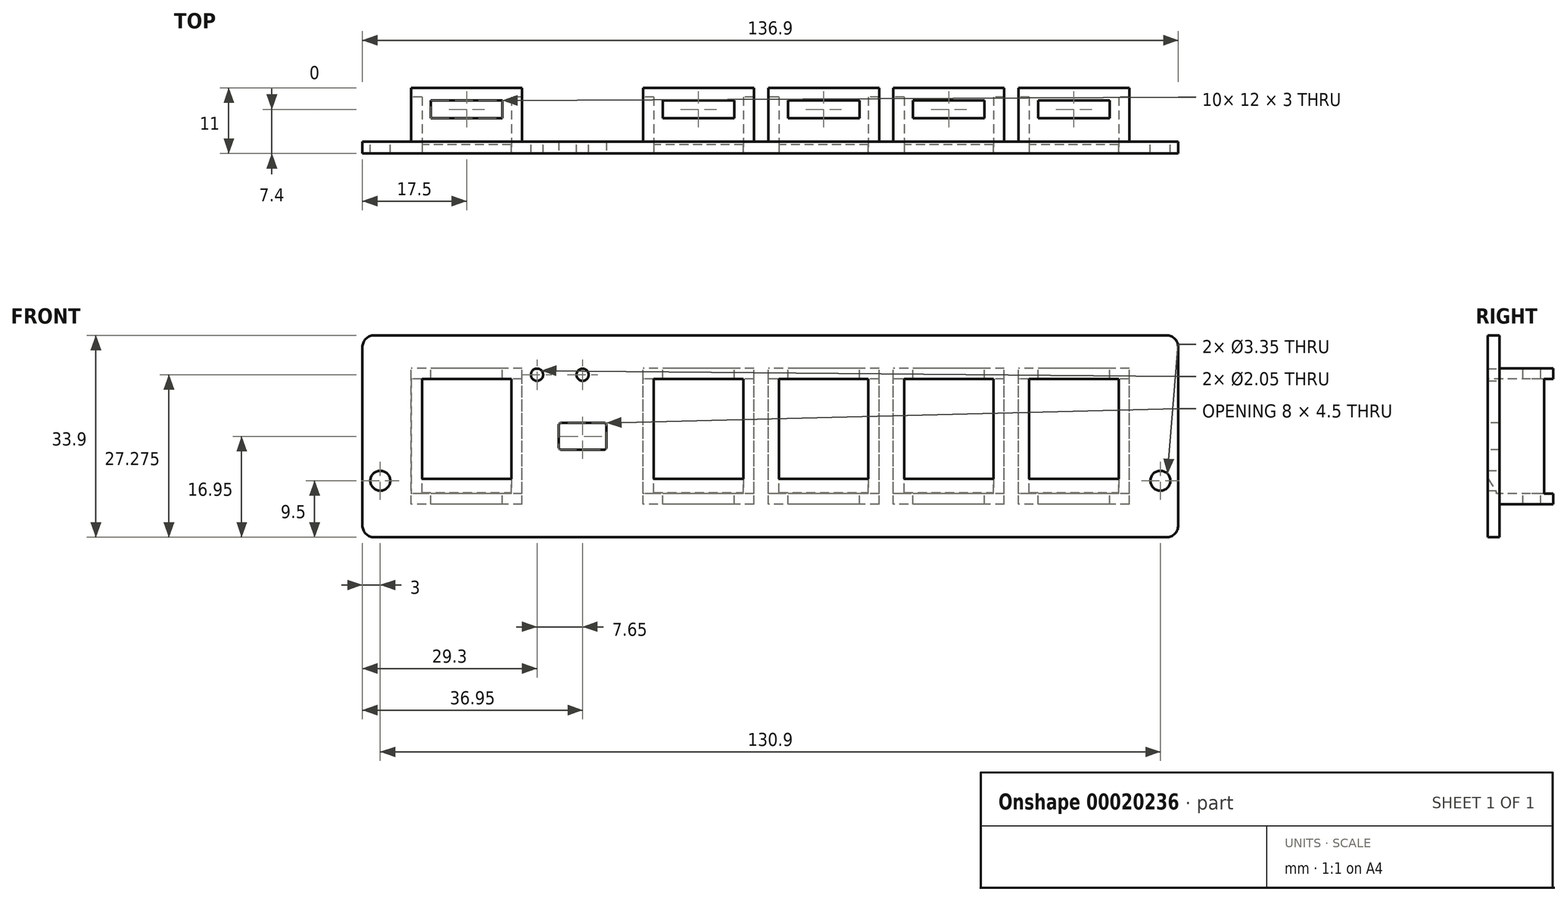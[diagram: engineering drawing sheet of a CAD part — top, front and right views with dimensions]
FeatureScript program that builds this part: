
annotation { "Feature Type Name" : "Feature", "Feature Type Description" : "" }
export const myFeature = defineFeature(function(context is Context, id is Id, definition is map)
    precondition{}
    {
        {
            var Q0;
            Q0=qCreatedBy(makeId("Front.planeOp"),FACE);
            var sketch = newSketch(context, id + "F0", { "sketchPlane" : qUnion([Q0])});
            skLineSegment(sketch, "E0.rect.bottom", {"start": v(66.45, -16.95) * mm, "end": v(-66.45, -16.95) * mm});
            skLineSegment(sketch, "E0.rect.top", {"start": v(66.45, 16.95) * mm, "end": v(-66.45, 16.95) * mm});
            skLineSegment(sketch, "E0.rect.left", {"start": v(68.45, -14.95) * mm, "end": v(68.45, 14.95) * mm});
            skLineSegment(sketch, "E0.rect.right", {"start": v(-68.45, -14.95) * mm, "end": v(-68.45, 14.95) * mm});
            skPoint(sketch, "E0.rect.middle", {"position": v(0, 0) * mm});
            skPoint(sketch, "E1.visualSharp", {"position": v(-68.45, 16.95) * mm});
            skArc(sketch, "E1.filletArc", {"start": v(-66.45, 16.95) * mm, "mid": v(-67.86, 16.36) * mm, "end": v(-68.45, 14.95) * mm});
            skPoint(sketch, "E2.visualSharp", {"position": v(68.45, 16.95) * mm});
            skArc(sketch, "E2.filletArc", {"start": v(68.45, 14.95) * mm, "mid": v(67.86, 16.36) * mm, "end": v(66.45, 16.95) * mm});
            skPoint(sketch, "E3.visualSharp", {"position": v(68.45, -16.95) * mm});
            skArc(sketch, "E3.filletArc", {"start": v(66.45, -16.95) * mm, "mid": v(67.86, -16.36) * mm, "end": v(68.45, -14.95) * mm});
            skPoint(sketch, "E4.visualSharp", {"position": v(-68.45, -16.95) * mm});
            skArc(sketch, "E4.filletArc", {"start": v(-68.45, -14.95) * mm, "mid": v(-67.86, -16.36) * mm, "end": v(-66.45, -16.95) * mm});
            skLineSegment(sketch, "E5", {"start": v(-68.45, -7.45) * mm, "end": v(68.45, -7.45) * mm, "construction": true});
            skCircle(sketch, "E6", {"center": v(-65.45, -7.45) * mm, "radius": 1.68 * mm});
            skCircle(sketch, "E7.MirrorC", {"center": v(65.45, -7.45) * mm, "radius": 1.68 * mm});
            skSolve(sketch);
        }
        {
            var Q0;
            Q0 = qSketchRegion(id + "F0", true);
            extrude(context, id + "F1", {"entities" : qUnion([Q0]), "depth" : 2 * mm});
        }
        {
            var Q0;
            Q0=makeQuery(id+"F1.opExtrude","CAP_FACE",FACE,{"disambiguationData":[OSD([sQuery(id+"F0.wireOp",EDGE,"E0.rect.bottom"),sQuery(id+"F0.wireOp",EDGE,"E0.rect.top"),sQuery(id+"F0.wireOp",EDGE,"E0.rect.left"),sQuery(id+"F0.wireOp",EDGE,"E0.rect.right"),sQuery(id+"F0.wireOp",EDGE,"E1.filletArc"),sQuery(id+"F0.wireOp",EDGE,"E2.filletArc"),sQuery(id+"F0.wireOp",EDGE,"E3.filletArc"),sQuery(id+"F0.wireOp",EDGE,"E4.filletArc"),sQuery(id+"F0.wireOp",EDGE,"E6"),sQuery(id+"F0.wireOp",EDGE,"E7.MirrorC")])],"isStart":false});
            var sketch = newSketch(context, id + "F2", { "sketchPlane" : qUnion([Q0])});
            skLineSegment(sketch, "E8.rect.bottom", {"start": v(58.45, -9.63) * mm, "end": v(43.45, -9.63) * mm});
            skLineSegment(sketch, "E8.rect.top", {"start": v(58.45, 9.62) * mm, "end": v(43.45, 9.62) * mm});
            skLineSegment(sketch, "E8.rect.left", {"start": v(58.45, -9.63) * mm, "end": v(58.45, 9.62) * mm});
            skLineSegment(sketch, "E8.rect.right", {"start": v(43.45, -9.63) * mm, "end": v(43.45, 9.62) * mm});
            skPoint(sketch, "E8.rect.middle", {"position": v(50.95, 0) * mm});
            skLineSegment(sketch, "E9.1.0.0", {"start": v(37.45, 9.62) * mm, "end": v(22.45, 9.62) * mm});
            skLineSegment(sketch, "E9.1.0.1", {"start": v(22.45, -9.63) * mm, "end": v(22.45, 9.62) * mm});
            skLineSegment(sketch, "E9.1.0.2", {"start": v(37.45, -9.63) * mm, "end": v(22.45, -9.63) * mm});
            skLineSegment(sketch, "E9.1.0.3", {"start": v(37.45, -9.63) * mm, "end": v(37.45, 9.62) * mm});
            skLineSegment(sketch, "E9.2.0.0", {"start": v(16.45, 9.62) * mm, "end": v(1.45, 9.62) * mm});
            skLineSegment(sketch, "E9.2.0.1", {"start": v(1.45, -9.63) * mm, "end": v(1.45, 9.62) * mm});
            skLineSegment(sketch, "E9.2.0.2", {"start": v(16.45, -9.63) * mm, "end": v(1.45, -9.63) * mm});
            skLineSegment(sketch, "E9.2.0.3", {"start": v(16.45, -9.63) * mm, "end": v(16.45, 9.62) * mm});
            skLineSegment(sketch, "E9.3.0.0", {"start": v(-4.55, 9.62) * mm, "end": v(-19.55, 9.62) * mm});
            skLineSegment(sketch, "E9.3.0.1", {"start": v(-19.55, -9.63) * mm, "end": v(-19.55, 9.62) * mm});
            skLineSegment(sketch, "E9.3.0.2", {"start": v(-4.55, -9.63) * mm, "end": v(-19.55, -9.63) * mm});
            skLineSegment(sketch, "E9.3.0.3", {"start": v(-4.55, -9.63) * mm, "end": v(-4.55, 9.62) * mm});
            skLineSegment(sketch, "E9.direction1", {"start": v(43.45, 9.62) * mm, "end": v(22.45, 9.62) * mm, "construction": true});
            skLineSegment(sketch, "E10.rect.bottom", {"start": v(-43.45, -9.63) * mm, "end": v(-58.45, -9.63) * mm});
            skLineSegment(sketch, "E10.rect.top", {"start": v(-43.45, 9.63) * mm, "end": v(-58.45, 9.63) * mm});
            skLineSegment(sketch, "E10.rect.left", {"start": v(-43.45, -9.63) * mm, "end": v(-43.45, 9.63) * mm});
            skLineSegment(sketch, "E10.rect.right", {"start": v(-58.45, -9.63) * mm, "end": v(-58.45, 9.63) * mm});
            skPoint(sketch, "E10.rect.middle", {"position": v(-50.95, 0) * mm});
            skSolve(sketch);
        }
        {
            var Q0;
            Q0 = qSketchRegion(id + "F2", true);
            extrude(context, id + "F3", {"entities" : qUnion([Q0]), "operationType" : NewBodyOperationType.REMOVE, "endBound" : BoundingType.THROUGH_ALL, "oppositeDirection" : true, "depth" : 25 * mm});
        }
        {
            var Q0;
            Q0=makeQuery(id+"F1.opExtrude","CAP_FACE",FACE,{"disambiguationData":[OSD([sQuery(id+"F0.wireOp",EDGE,"E0.rect.bottom"),sQuery(id+"F0.wireOp",EDGE,"E0.rect.top"),sQuery(id+"F0.wireOp",EDGE,"E0.rect.left"),sQuery(id+"F0.wireOp",EDGE,"E0.rect.right"),sQuery(id+"F0.wireOp",EDGE,"E1.filletArc"),sQuery(id+"F0.wireOp",EDGE,"E2.filletArc"),sQuery(id+"F0.wireOp",EDGE,"E3.filletArc"),sQuery(id+"F0.wireOp",EDGE,"E4.filletArc"),sQuery(id+"F0.wireOp",EDGE,"E6"),sQuery(id+"F0.wireOp",EDGE,"E7.MirrorC")])],"isStart":true});
            var sketch = newSketch(context, id + "F4", { "sketchPlane" : qUnion([Q0])});
            skLineSegment(sketch, "E11.0", {"start": v(-60.25, 11.42) * mm, "end": v(-41.65, 11.42) * mm});
            skLineSegment(sketch, "E11.1", {"start": v(-60.25, -11.43) * mm, "end": v(-60.25, 11.42) * mm});
            skLineSegment(sketch, "E11.2", {"start": v(-60.25, -11.43) * mm, "end": v(-41.65, -11.43) * mm});
            skLineSegment(sketch, "E11.3", {"start": v(-41.65, -11.43) * mm, "end": v(-41.65, 11.42) * mm});
            skLineSegment(sketch, "E12.0", {"start": v(-39.25, 11.42) * mm, "end": v(-20.65, 11.42) * mm});
            skLineSegment(sketch, "E12.1", {"start": v(-39.25, -11.43) * mm, "end": v(-39.25, 11.42) * mm});
            skLineSegment(sketch, "E12.2", {"start": v(-39.25, -11.43) * mm, "end": v(-20.65, -11.43) * mm});
            skLineSegment(sketch, "E12.3", {"start": v(-20.65, -11.43) * mm, "end": v(-20.65, 11.42) * mm});
            skLineSegment(sketch, "E13.0", {"start": v(-18.25, 11.42) * mm, "end": v(0.35, 11.42) * mm});
            skLineSegment(sketch, "E13.1", {"start": v(-18.25, -11.43) * mm, "end": v(-18.25, 11.42) * mm});
            skLineSegment(sketch, "E13.2", {"start": v(-18.25, -11.43) * mm, "end": v(0.35, -11.43) * mm});
            skLineSegment(sketch, "E13.3", {"start": v(0.35, -11.43) * mm, "end": v(0.35, 11.42) * mm});
            skLineSegment(sketch, "E14.0", {"start": v(2.75, 11.42) * mm, "end": v(21.35, 11.42) * mm});
            skLineSegment(sketch, "E14.1", {"start": v(2.75, -11.43) * mm, "end": v(2.75, 11.42) * mm});
            skLineSegment(sketch, "E14.2", {"start": v(2.75, -11.43) * mm, "end": v(21.35, -11.43) * mm});
            skLineSegment(sketch, "E14.3", {"start": v(21.35, -11.43) * mm, "end": v(21.35, 11.42) * mm});
            skLineSegment(sketch, "E15.0", {"start": v(41.65, 11.43) * mm, "end": v(60.25, 11.43) * mm});
            skLineSegment(sketch, "E15.1", {"start": v(41.65, -11.43) * mm, "end": v(41.65, 11.43) * mm});
            skLineSegment(sketch, "E15.2", {"start": v(41.65, -11.43) * mm, "end": v(60.25, -11.43) * mm});
            skLineSegment(sketch, "E15.3", {"start": v(60.25, -11.43) * mm, "end": v(60.25, 11.43) * mm});
            skLineSegment(sketch, "E16.0", {"start": v(-58.45, 9.62) * mm, "end": v(-43.45, 9.62) * mm});
            skLineSegment(sketch, "E16.1", {"start": v(-58.45, -9.63) * mm, "end": v(-58.45, 9.62) * mm});
            skLineSegment(sketch, "E16.2", {"start": v(-58.45, -9.63) * mm, "end": v(-43.45, -9.63) * mm});
            skLineSegment(sketch, "E16.3", {"start": v(-43.45, -9.63) * mm, "end": v(-43.45, 9.62) * mm});
            skLineSegment(sketch, "E17.0", {"start": v(-37.45, 9.62) * mm, "end": v(-22.45, 9.62) * mm});
            skLineSegment(sketch, "E17.1", {"start": v(-37.45, -9.63) * mm, "end": v(-37.45, 9.62) * mm});
            skLineSegment(sketch, "E17.2", {"start": v(-37.45, -9.63) * mm, "end": v(-22.45, -9.63) * mm});
            skLineSegment(sketch, "E17.3", {"start": v(-22.45, -9.63) * mm, "end": v(-22.45, 9.62) * mm});
            skLineSegment(sketch, "E18.0", {"start": v(-16.45, -9.63) * mm, "end": v(-16.45, 9.62) * mm});
            skLineSegment(sketch, "E18.1", {"start": v(-16.45, -9.63) * mm, "end": v(-1.45, -9.63) * mm});
            skLineSegment(sketch, "E18.2", {"start": v(-1.45, -9.63) * mm, "end": v(-1.45, 9.62) * mm});
            skLineSegment(sketch, "E18.3", {"start": v(-16.45, 9.62) * mm, "end": v(-1.45, 9.62) * mm});
            skLineSegment(sketch, "E19.0", {"start": v(4.55, -9.63) * mm, "end": v(4.55, 9.62) * mm});
            skLineSegment(sketch, "E19.1", {"start": v(4.55, -9.63) * mm, "end": v(19.55, -9.63) * mm});
            skLineSegment(sketch, "E19.2", {"start": v(19.55, -9.63) * mm, "end": v(19.55, 9.62) * mm});
            skLineSegment(sketch, "E19.3", {"start": v(4.55, 9.62) * mm, "end": v(19.55, 9.62) * mm});
            skLineSegment(sketch, "E20.0", {"start": v(43.45, -9.63) * mm, "end": v(43.45, 9.63) * mm});
            skLineSegment(sketch, "E20.1", {"start": v(43.45, -9.63) * mm, "end": v(58.45, -9.63) * mm});
            skLineSegment(sketch, "E20.2", {"start": v(58.45, -9.63) * mm, "end": v(58.45, 9.63) * mm});
            skLineSegment(sketch, "E20.3", {"start": v(43.45, 9.63) * mm, "end": v(58.45, 9.63) * mm});
            skSolve(sketch);
        }
        {
            var Q0;
            Q0 = qSketchRegion(id + "F4", true);
            extrude(context, id + "F5", {"entities" : qUnion([Q0]), "operationType" : NewBodyOperationType.ADD, "depth" : 9 * mm});
        }
        {
            var Q0;
            Q0=makeQuery(id+"F5.opExtrude","SWEPT_FACE",FACE,{"disambiguationData":[OSD([sQuery(id+"F4.wireOp",EDGE,"E11.2")])]});
            var sketch = newSketch(context, id + "F6", { "sketchPlane" : qUnion([Q0])});
            skLineSegment(sketch, "E21", {"start": v(50.95, -9) * mm, "end": v(50.95, 0) * mm, "construction": true});
            skLineSegment(sketch, "E22.rect.bottom", {"start": v(56.95, -6.9) * mm, "end": v(44.95, -6.9) * mm});
            skLineSegment(sketch, "E22.rect.top", {"start": v(56.95, -3.9) * mm, "end": v(44.95, -3.9) * mm});
            skLineSegment(sketch, "E22.rect.left", {"start": v(56.95, -6.9) * mm, "end": v(56.95, -3.9) * mm});
            skLineSegment(sketch, "E22.rect.right", {"start": v(44.95, -6.9) * mm, "end": v(44.95, -3.9) * mm});
            skPoint(sketch, "E22.rect.middle", {"position": v(50.95, -5.4) * mm});
            skLineSegment(sketch, "E23.1.0.0", {"start": v(23.95, -6.9) * mm, "end": v(23.95, -3.9) * mm});
            skLineSegment(sketch, "E23.1.0.1", {"start": v(35.95, -3.9) * mm, "end": v(23.95, -3.9) * mm});
            skLineSegment(sketch, "E23.1.0.2", {"start": v(35.95, -6.9) * mm, "end": v(23.95, -6.9) * mm});
            skLineSegment(sketch, "E23.1.0.3", {"start": v(35.95, -6.9) * mm, "end": v(35.95, -3.9) * mm});
            skLineSegment(sketch, "E23.2.0.0", {"start": v(2.95, -6.9) * mm, "end": v(2.95, -3.9) * mm});
            skLineSegment(sketch, "E23.2.0.1", {"start": v(14.95, -3.9) * mm, "end": v(2.95, -3.9) * mm});
            skLineSegment(sketch, "E23.2.0.2", {"start": v(14.95, -6.9) * mm, "end": v(2.95, -6.9) * mm});
            skLineSegment(sketch, "E23.2.0.3", {"start": v(14.95, -6.9) * mm, "end": v(14.95, -3.9) * mm});
            skLineSegment(sketch, "E23.3.0.0", {"start": v(-18.05, -6.9) * mm, "end": v(-18.05, -3.9) * mm});
            skLineSegment(sketch, "E23.3.0.1", {"start": v(-6.05, -3.9) * mm, "end": v(-18.05, -3.9) * mm});
            skLineSegment(sketch, "E23.3.0.2", {"start": v(-6.05, -6.9) * mm, "end": v(-18.05, -6.9) * mm});
            skLineSegment(sketch, "E23.3.0.3", {"start": v(-6.05, -6.9) * mm, "end": v(-6.05, -3.9) * mm});
            skLineSegment(sketch, "E23.direction1", {"start": v(44.95, -6.9) * mm, "end": v(23.95, -6.9) * mm, "construction": true});
            skLineSegment(sketch, "E24", {"start": v(-50.95, -9) * mm, "end": v(-50.95, 0) * mm, "construction": true});
            skLineSegment(sketch, "E25.rect.bottom", {"start": v(-44.95, -6.9) * mm, "end": v(-56.95, -6.9) * mm});
            skLineSegment(sketch, "E25.rect.top", {"start": v(-44.95, -3.9) * mm, "end": v(-56.95, -3.9) * mm});
            skLineSegment(sketch, "E25.rect.left", {"start": v(-44.95, -6.9) * mm, "end": v(-44.95, -3.9) * mm});
            skLineSegment(sketch, "E25.rect.right", {"start": v(-56.95, -6.9) * mm, "end": v(-56.95, -3.9) * mm});
            skPoint(sketch, "E25.rect.middle", {"position": v(-50.95, -5.4) * mm});
            skSolve(sketch);
        }
        {
            var Q0;
            Q0 = qSketchRegion(id + "F6", true);
            extrude(context, id + "F7", {"entities" : qUnion([Q0]), "operationType" : NewBodyOperationType.REMOVE, "endBound" : BoundingType.THROUGH_ALL, "depth" : 25 * mm, "hasSecondDirection" : true, "secondDirectionOppositeDirection" : true, "secondDirectionDepth" : 25 * mm});
        }
        {
            var Q0;
            Q0=makeQuery(id+"F5.opExtrude","CAP_FACE",FACE,{"disambiguationData":[OSD([sQuery(id+"F4.wireOp",EDGE,"E11.0"),sQuery(id+"F4.wireOp",EDGE,"E11.1"),sQuery(id+"F4.wireOp",EDGE,"E11.2"),sQuery(id+"F4.wireOp",EDGE,"E11.3"),sQuery(id+"F4.wireOp",EDGE,"E16.0"),sQuery(id+"F4.wireOp",EDGE,"E16.1"),sQuery(id+"F4.wireOp",EDGE,"E16.2"),sQuery(id+"F4.wireOp",EDGE,"E16.3")])],"isStart":false});
            var sketch = newSketch(context, id + "F8", { "sketchPlane" : qUnion([Q0])});
            skLineSegment(sketch, "E26.bottom", {"start": v(-60.25, 9.62) * mm, "end": v(60.25, 9.62) * mm});
            skLineSegment(sketch, "E26.top", {"start": v(-60.25, -9.63) * mm, "end": v(60.25, -9.63) * mm});
            skLineSegment(sketch, "E26.left", {"start": v(-60.25, 9.62) * mm, "end": v(-60.25, -9.63) * mm});
            skLineSegment(sketch, "E26.right", {"start": v(60.25, 9.62) * mm, "end": v(60.25, -9.63) * mm});
            skSolve(sketch);
        }
        {
            var Q0;
            Q0 = qSketchRegion(id + "F8", true);
            var Q1;
            Q1=makeQuery(id+"F1.opExtrude","CAP_FACE",FACE,{"disambiguationData":[OSD([sQuery(id+"F0.wireOp",EDGE,"E0.rect.bottom"),sQuery(id+"F0.wireOp",EDGE,"E0.rect.top"),sQuery(id+"F0.wireOp",EDGE,"E0.rect.left"),sQuery(id+"F0.wireOp",EDGE,"E0.rect.right"),sQuery(id+"F0.wireOp",EDGE,"E1.filletArc"),sQuery(id+"F0.wireOp",EDGE,"E2.filletArc"),sQuery(id+"F0.wireOp",EDGE,"E3.filletArc"),sQuery(id+"F0.wireOp",EDGE,"E4.filletArc"),sQuery(id+"F0.wireOp",EDGE,"E6"),sQuery(id+"F0.wireOp",EDGE,"E7.MirrorC")])],"isStart":false});
            extrude(context, id + "F9", {"entities" : qUnion([Q0]), "operationType" : NewBodyOperationType.REMOVE, "oppositeDirection" : true, "endBoundEntityFace" : qUnion([Q1]), "depth" : 1.5 * mm});
        }
        {
            var Q0;
            Q0=makeQuery(id+"F1.opExtrude","CAP_FACE",FACE,{"disambiguationData":[OSD([sQuery(id+"F0.wireOp",EDGE,"E0.rect.bottom"),sQuery(id+"F0.wireOp",EDGE,"E0.rect.top"),sQuery(id+"F0.wireOp",EDGE,"E0.rect.left"),sQuery(id+"F0.wireOp",EDGE,"E0.rect.right"),sQuery(id+"F0.wireOp",EDGE,"E1.filletArc"),sQuery(id+"F0.wireOp",EDGE,"E2.filletArc"),sQuery(id+"F0.wireOp",EDGE,"E3.filletArc"),sQuery(id+"F0.wireOp",EDGE,"E4.filletArc"),sQuery(id+"F0.wireOp",EDGE,"E6"),sQuery(id+"F0.wireOp",EDGE,"E7.MirrorC")])],"isStart":false});
            var sketch = newSketch(context, id + "F10", { "sketchPlane" : qUnion([Q0])});
            skLineSegment(sketch, "E27", {"start": v(-43.45, 0) * mm, "end": v(-19.55, 0) * mm, "construction": true});
            skLineSegment(sketch, "E28.rect.bottom", {"start": v(-27.9, -2.25) * mm, "end": v(-35.1, -2.25) * mm});
            skLineSegment(sketch, "E28.rect.top", {"start": v(-27.9, 2.25) * mm, "end": v(-35.1, 2.25) * mm});
            skLineSegment(sketch, "E28.rect.left", {"start": v(-27.5, -1.85) * mm, "end": v(-27.5, 1.85) * mm});
            skLineSegment(sketch, "E28.rect.right", {"start": v(-35.5, -1.85) * mm, "end": v(-35.5, 1.85) * mm});
            skPoint(sketch, "E28.rect.middle", {"position": v(-31.5, 0) * mm});
            skPoint(sketch, "E29.visualSharp", {"position": v(-35.5, 2.25) * mm});
            skArc(sketch, "E29.filletArc", {"start": v(-35.1, 2.25) * mm, "mid": v(-35.38, 2.13) * mm, "end": v(-35.5, 1.85) * mm});
            skPoint(sketch, "E30.visualSharp", {"position": v(-27.5, 2.25) * mm});
            skArc(sketch, "E30.filletArc", {"start": v(-27.5, 1.85) * mm, "mid": v(-27.62, 2.13) * mm, "end": v(-27.9, 2.25) * mm});
            skPoint(sketch, "E31.visualSharp", {"position": v(-27.5, -2.25) * mm});
            skArc(sketch, "E31.filletArc", {"start": v(-27.9, -2.25) * mm, "mid": v(-27.62, -2.13) * mm, "end": v(-27.5, -1.85) * mm});
            skPoint(sketch, "E32.visualSharp", {"position": v(-35.5, -2.25) * mm});
            skArc(sketch, "E32.filletArc", {"start": v(-35.5, -1.85) * mm, "mid": v(-35.38, -2.13) * mm, "end": v(-35.1, -2.25) * mm});
            skSolve(sketch);
        }
        {
            var Q0;
            Q0 = qSketchRegion(id + "F10", true);
            extrude(context, id + "F11", {"entities" : qUnion([Q0]), "operationType" : NewBodyOperationType.REMOVE, "oppositeDirection" : true, "depth" : 25 * mm});
        }
        {
            var Q0;
            Q0=makeQuery(id+"F1.opExtrude","CAP_FACE",FACE,{"disambiguationData":[OSD([sQuery(id+"F0.wireOp",EDGE,"E0.rect.bottom"),sQuery(id+"F0.wireOp",EDGE,"E0.rect.top"),sQuery(id+"F0.wireOp",EDGE,"E0.rect.left"),sQuery(id+"F0.wireOp",EDGE,"E0.rect.right"),sQuery(id+"F0.wireOp",EDGE,"E1.filletArc"),sQuery(id+"F0.wireOp",EDGE,"E2.filletArc"),sQuery(id+"F0.wireOp",EDGE,"E3.filletArc"),sQuery(id+"F0.wireOp",EDGE,"E4.filletArc"),sQuery(id+"F0.wireOp",EDGE,"E6"),sQuery(id+"F0.wireOp",EDGE,"E7.MirrorC")])],"isStart":false});
            var sketch = newSketch(context, id + "F12", { "sketchPlane" : qUnion([Q0])});
            skLineSegment(sketch, "E33.bottom", {"start": v(-58.45, -9.63) * mm, "end": v(-43.45, -9.63) * mm});
            skLineSegment(sketch, "E33.top", {"start": v(-58.45, -7.13) * mm, "end": v(-43.45, -7.13) * mm});
            skLineSegment(sketch, "E33.left", {"start": v(-58.45, -9.63) * mm, "end": v(-58.45, -7.13) * mm});
            skLineSegment(sketch, "E33.right", {"start": v(-43.45, -9.63) * mm, "end": v(-43.45, -7.13) * mm});
            skLineSegment(sketch, "E34.bottom", {"start": v(-19.55, -9.63) * mm, "end": v(-4.55, -9.63) * mm});
            skLineSegment(sketch, "E34.top", {"start": v(-19.55, -7.13) * mm, "end": v(-4.55, -7.13) * mm});
            skLineSegment(sketch, "E34.left", {"start": v(-19.55, -9.63) * mm, "end": v(-19.55, -7.13) * mm});
            skLineSegment(sketch, "E34.right", {"start": v(-4.55, -9.63) * mm, "end": v(-4.55, -7.13) * mm});
            skLineSegment(sketch, "E35.bottom", {"start": v(1.45, -9.63) * mm, "end": v(16.45, -9.63) * mm});
            skLineSegment(sketch, "E35.top", {"start": v(1.45, -7.13) * mm, "end": v(16.45, -7.13) * mm});
            skLineSegment(sketch, "E35.left", {"start": v(1.45, -9.63) * mm, "end": v(1.45, -7.13) * mm});
            skLineSegment(sketch, "E35.right", {"start": v(16.45, -9.63) * mm, "end": v(16.45, -7.13) * mm});
            skLineSegment(sketch, "E36.bottom", {"start": v(22.45, -9.63) * mm, "end": v(37.45, -9.63) * mm});
            skLineSegment(sketch, "E36.top", {"start": v(22.45, -7.13) * mm, "end": v(37.45, -7.13) * mm});
            skLineSegment(sketch, "E36.left", {"start": v(22.45, -9.63) * mm, "end": v(22.45, -7.13) * mm});
            skLineSegment(sketch, "E36.right", {"start": v(37.45, -9.63) * mm, "end": v(37.45, -7.13) * mm});
            skLineSegment(sketch, "E37.bottom", {"start": v(43.45, -9.63) * mm, "end": v(58.45, -9.63) * mm});
            skLineSegment(sketch, "E37.top", {"start": v(43.45, -7.13) * mm, "end": v(58.45, -7.13) * mm});
            skLineSegment(sketch, "E37.left", {"start": v(43.45, -9.63) * mm, "end": v(43.45, -7.13) * mm});
            skLineSegment(sketch, "E37.right", {"start": v(58.45, -9.63) * mm, "end": v(58.45, -7.13) * mm});
            skSolve(sketch);
        }
        {
            var Q0;
            Q0 = qSketchRegion(id + "F12", true);
            extrude(context, id + "F13", {"entities" : qUnion([Q0]), "operationType" : NewBodyOperationType.ADD, "oppositeDirection" : true, "depth" : 1.5 * mm});
        }
        {
            var Q0;
            Q0=makeQuery(id+"F13.opExtrude","CAP_EDGE",EDGE,{"disambiguationData":[OSD([sQuery(id+"F12.wireOp",EDGE,"E37.top")])],"isStart":false});
            var Q1;
            Q1=makeQuery(id+"F13.opExtrude","CAP_EDGE",EDGE,{"disambiguationData":[OSD([sQuery(id+"F12.wireOp",EDGE,"E36.top")])],"isStart":false});
            var Q2;
            Q2=makeQuery(id+"F13.opExtrude","CAP_EDGE",EDGE,{"disambiguationData":[OSD([sQuery(id+"F12.wireOp",EDGE,"E35.top")])],"isStart":false});
            var Q3;
            Q3=makeQuery(id+"F13.opExtrude","CAP_EDGE",EDGE,{"disambiguationData":[OSD([sQuery(id+"F12.wireOp",EDGE,"E34.top")])],"isStart":false});
            var Q4;
            Q4=makeQuery(id+"F13.opExtrude","CAP_EDGE",EDGE,{"disambiguationData":[OSD([sQuery(id+"F12.wireOp",EDGE,"E33.top")])],"isStart":false});
            chamfer(context, id + "F14", {"entities" : qUnion([Q0, Q1, Q2, Q3, Q4]), "chamferType" : ChamferType.TWO_OFFSETS, "width1" : 2.3 * mm, "oppositeDirection" : false, "width2" : 1.4 * mm, "tangentPropagation" : true});
        }
        {
            var Q0;
            Q0=makeQuery(id+"F1.opExtrude","CAP_FACE",FACE,{"disambiguationData":[OSD([sQuery(id+"F0.wireOp",EDGE,"E0.rect.bottom"),sQuery(id+"F0.wireOp",EDGE,"E0.rect.top"),sQuery(id+"F0.wireOp",EDGE,"E0.rect.left"),sQuery(id+"F0.wireOp",EDGE,"E0.rect.right"),sQuery(id+"F0.wireOp",EDGE,"E1.filletArc"),sQuery(id+"F0.wireOp",EDGE,"E2.filletArc"),sQuery(id+"F0.wireOp",EDGE,"E3.filletArc"),sQuery(id+"F0.wireOp",EDGE,"E4.filletArc"),sQuery(id+"F0.wireOp",EDGE,"E6"),sQuery(id+"F0.wireOp",EDGE,"E7.MirrorC")])],"isStart":true});
            var sketch = newSketch(context, id + "F15", { "sketchPlane" : qUnion([Q0])});
            skCircle(sketch, "E38", {"center": v(39.15, 10.32) * mm, "radius": 1.02 * mm});
            skLineSegment(sketch, "E39", {"start": v(31.5, 2.25) * mm, "end": v(31.5, 16.95) * mm, "construction": true});
            skCircle(sketch, "E40", {"center": v(31.5, 10.32) * mm, "radius": 1.02 * mm});
            skLineSegment(sketch, "E41", {"start": v(31.5, 10.32) * mm, "end": v(39.15, 10.32) * mm, "construction": true});
            skSolve(sketch);
        }
        {
            var Q0;
            Q0 = qSketchRegion(id + "F15", true);
            extrude(context, id + "F16", {"entities" : qUnion([Q0]), "operationType" : NewBodyOperationType.REMOVE, "endBound" : BoundingType.THROUGH_ALL, "oppositeDirection" : true, "depth" : 25 * mm});
        }
    });
